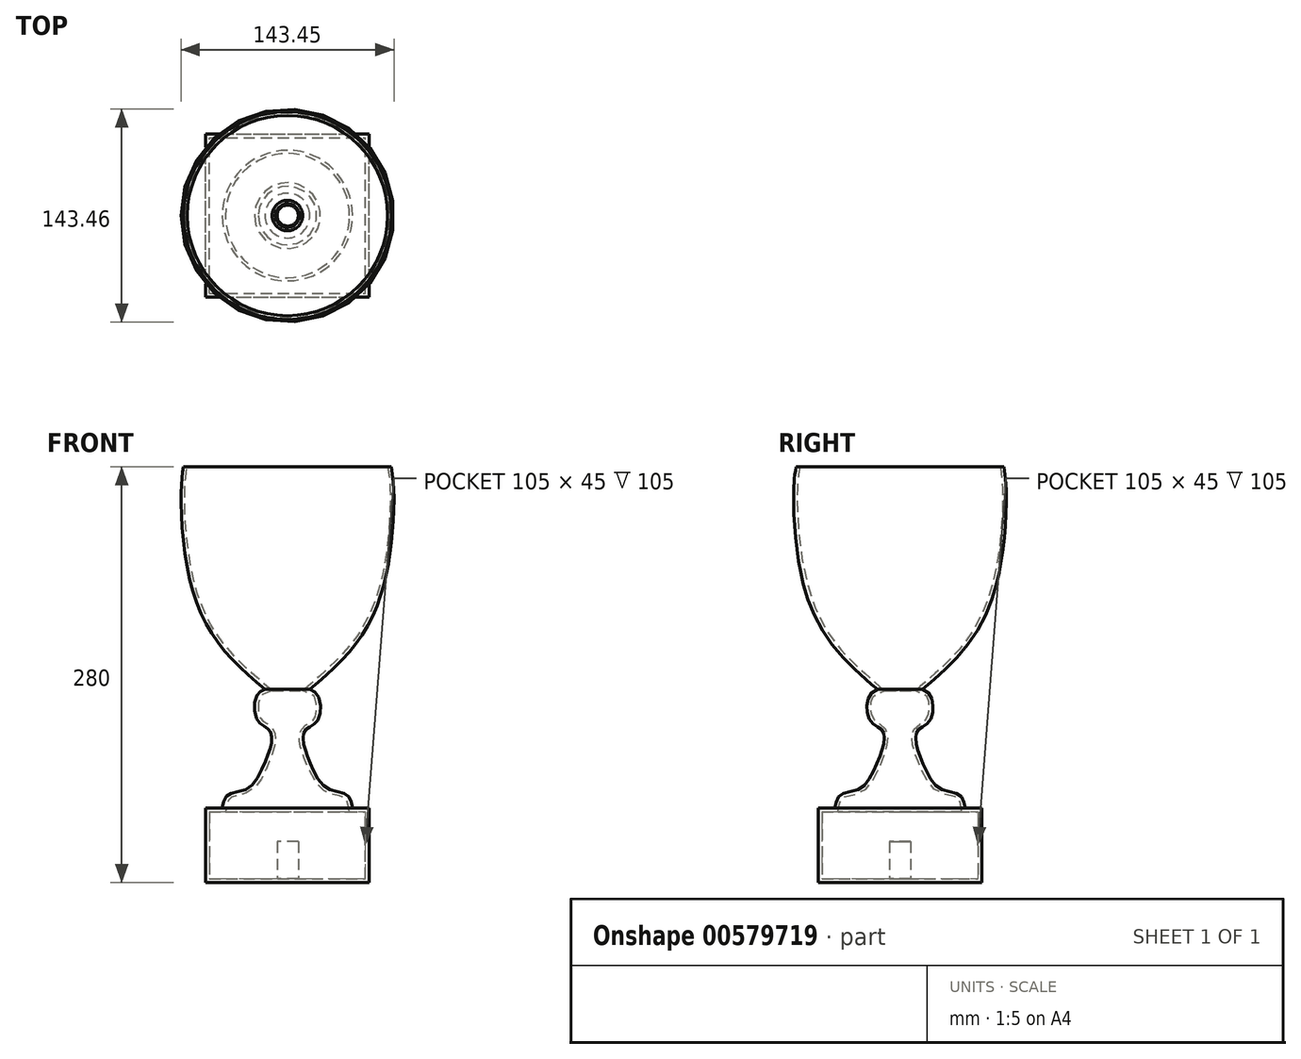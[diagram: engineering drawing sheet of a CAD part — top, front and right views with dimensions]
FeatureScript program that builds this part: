
annotation { "Feature Type Name" : "Feature", "Feature Type Description" : "" }
export const myFeature = defineFeature(function(context is Context, id is Id, definition is map)
    precondition{}
    {
        {
            var Q0;
            Q0=qCreatedBy(makeId("Front.planeOp"),FACE);
            var sketch = newSketch(context, id + "F0", { "sketchPlane" : qUnion([Q0])});
            skLineSegment(sketch, "E0", {"start": v(0, 0) * mm, "end": v(110, 0) * mm});
            skLineSegment(sketch, "E1", {"start": v(0, 0) * mm, "end": v(0, -50) * mm});
            skLineSegment(sketch, "E2", {"start": v(0, -50) * mm, "end": v(110, -50) * mm});
            skLineSegment(sketch, "E3", {"start": v(110, -50) * mm, "end": v(110, 0) * mm});
            skSolve(sketch);
        }
        {
            var Q0;
            Q0 = qSketchRegion(id + "F0", true);
            extrude(context, id + "F1", {"entities" : qUnion([Q0]), "endBound" : BoundingType.SYMMETRIC, "depth" : 110 * mm, "offsetDistance" : 25 * mm});
        }
        {
            var Q0;
            Q0=qCreatedBy(makeId("Front.planeOp"),FACE);
            var sketch = newSketch(context, id + "F2", { "sketchPlane" : qUnion([Q0])});
            skLineSegment(sketch, "E4", {"start": v(0, 0) * mm, "end": v(55, 0) * mm});
            skLineSegment(sketch, "E5", {"start": v(55, 0) * mm, "end": v(55, 230) * mm});
            skLineSegment(sketch, "E6", {"start": v(55, 230) * mm, "end": v(-15, 230) * mm});
            skLineSegment(sketch, "E7", {"start": v(55, 0) * mm, "end": v(55, 80) * mm});
            skFitSpline(sketch, "E8", {"points": [v(39.9, 80) * mm, v(7.12, 113.12) * mm, v(-12.1, 160.05) * mm, v(-16.63, 214.9) * mm, v(-15, 230) * mm], "startDerivative": vector(-132.2, 114.52) * mm, "endDerivative": vector(13.45, 80.65) * mm});
            skLineSegment(sketch, "E9", {"start": v(55, 0) * mm, "end": v(55, 60) * mm});
            skFitSpline(sketch, "E10", {"points": [v(39.9, 80) * mm, v(34.25, 75.81) * mm, v(34.25, 60) * mm, v(39.9, 54.9) * mm, v(43.87, 50.93) * mm, v(43.87, 42.45) * mm, v(39.9, 31.15) * mm, v(28.6, 13.62) * mm, v(15.03, 9.1) * mm, v(11.07, 0) * mm], "startDerivative": vector(-72.87, -27.02) * mm, "endDerivative": vector(-19.03, -102.8) * mm});
            skLineSegment(sketch, "E11", {"start": v(11.07, 0) * mm, "end": v(55, 0) * mm});
            skSolve(sketch);
        }
        {
            var Q0;
            Q0=makeQuery(id+"F2.imprint","IMPRINT",FACE,{"disambiguationData":[TD([[makeQuery(id+"F2.imprint","IMPRINT",EDGE,{"derivedFrom":sQuery(id+"F2.wireOp",EDGE,"E5")}),1.0]])]});
            var Q1;
            Q1=sQuery(id+"F2.wireOp",EDGE,"E5");
            revolve(context, id + "F3", {"operationType" : NewBodyOperationType.ADD, "entities" : qUnion([Q0]), "axis" : qUnion([Q1]), "revolveType" : RevolveType.FULL});
        }
        {
            var Q0;
            Q0=makeQuery(id+"F3.opRevolve","SWEPT_FACE",FACE,{"disambiguationData":[OSD([sQuery(id+"F2.wireOp",EDGE,"E6")])]});
            shell(context, id + "F4", {"entities" : qUnion([Q0]), "thickness" : 2.5 * mm});
        }
        {
            var Q0;
            Q0=makeQuery(id+"F4.opShell","OFFSET_FACE",FACE,{"disambiguationData":[OSD([sQuery(id+"F0.wireOp",EDGE,"E2")])]});
            var sketch = newSketch(context, id + "F5", { "sketchPlane" : qUnion([Q0])});
            skCircle(sketch, "E12", {"center": v(55.17, 0) * mm, "radius": 7.14 * mm});
            skSolve(sketch);
        }
        {
            var Q0;
            Q0 = qSketchRegion(id + "F5", true);
            extrude(context, id + "F6", {"entities" : qUnion([Q0]), "operationType" : NewBodyOperationType.ADD, "depth" : 25 * mm, "offsetDistance" : 25 * mm});
        }
    });
